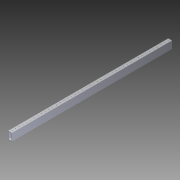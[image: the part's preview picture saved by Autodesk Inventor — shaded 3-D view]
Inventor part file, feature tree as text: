
AUTODESK INVENTOR PART (.ipt)
format: ipt  version: 2014 SP1 (Build 180222100, 222)  size: 772,608 bytes
history: native  units: in
note: dims shown in document units (in); Inventor stores cm internally (conversion verified against a paired STEP export)
features: other x2, extrude x1, imported_body x1, sketch x1
ambient origin geometry x8: Origin, YZ Plane, XZ Plane, XY Plane, X Axis, Y Axis, Z Axis, Center Point
bodies: Body1 (feature_tree)
feature tree (5):
  other  "Cut-Extrude2"
  other  "2x1 Tube1"
  extrude  "Extrusion1"  [1 undecoded]
  imported_body  "Base1"
  sketch  "Sketch1"  dims[d0=16.0in d1=0.0in]
note: 1 required parameter value undecoded (feature->parameter linkage not recoverable at this tier; creation-order binding heuristic only, values carry confidence <= 0.55)
